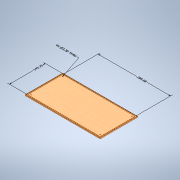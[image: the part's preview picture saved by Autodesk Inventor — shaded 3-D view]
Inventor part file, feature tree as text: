
AUTODESK INVENTOR PART (.ipt)
format: ipt  version: 2022 (Build 260153000, 153)  size: 170,496 bytes
history: native  units: mm
features: extrude x4, sketch x4, other x3, mirror x2, hole x1
ambient origin geometry x8: Origin, YZ Plane, XZ Plane, XY Plane, X Axis, Y Axis, Z Axis, Center Point
bodies: Solid1 (feature_tree)
feature tree (14):
  other  "Annotations"
  extrude  "Bottom_Base"  Depth=3.572mm
  extrude  "Side_Insert"  Depth=1.5875mm
  mirror  "Mirrored_Side_Insert"
  extrude  "Front_Insert"  Depth=3.572mm
  mirror  "Back_Insert"
  extrude  "Joint_Holes"  Depth=0.8mm TaperAngle=0.0deg
  sketch  "Sketch1"  dims[d2=0.0mm d3=3.572mm]
  sketch  "Sketch2"  dims[d4=1.5875mm d5=1.5875mm]
  sketch  "Sketch3"  dims[d6=0.8mm d7=0.0mm d8=3.572mm]
  sketch  "Sketch4"  dims[d9=1.5875mm d10=0.8mm d11=0.0mm d18=3.3mm d19=6.6mm d20=6.6mm d21=6.6mm d22=6.6mm d23=0.0mm d24=0.0mm d27=300.0mm d12=0.167694mm d13=0.260382mm d14=143.253mm d15=8.279997mm d16=0.523652mm d17=289.681mm d25=55.304283mm]
  other  "Linear Dimension 1"
  other  "Linear Dimension 2"
  hole  "Hole Note 1"  [1 undecoded]
note: 1 required parameter value undecoded (feature->parameter linkage not recoverable at this tier; creation-order binding heuristic only, values carry confidence <= 0.55)
